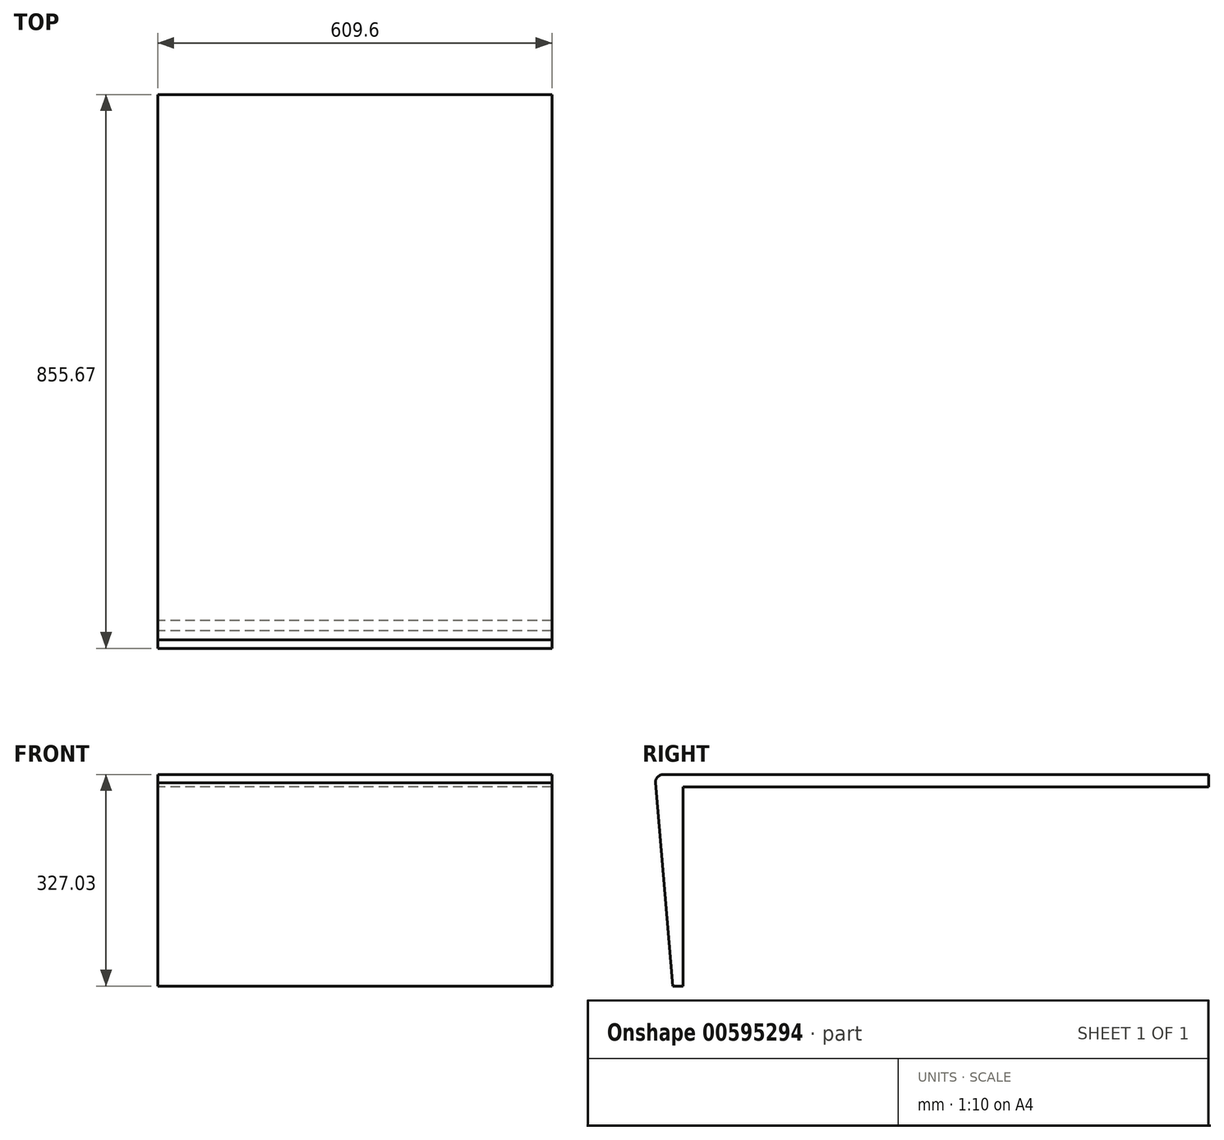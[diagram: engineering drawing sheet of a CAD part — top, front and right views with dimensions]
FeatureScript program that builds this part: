
annotation { "Feature Type Name" : "Feature", "Feature Type Description" : "" }
export const myFeature = defineFeature(function(context is Context, id is Id, definition is map)
    precondition{}
    {
        {
            var Q0;
            Q0=qCreatedBy(makeId("Right.planeOp"),FACE);
            var sketch = newSketch(context, id + "F0", { "sketchPlane" : qUnion([Q0])});
            skLineSegment(sketch, "E0", {"start": v(0, 0) * mm, "end": v(812.8, 0) * mm});
            skLineSegment(sketch, "E1", {"start": v(0, 0) * mm, "end": v(0, -307.98) * mm});
            skLineSegment(sketch, "E2", {"start": v(0, -307.98) * mm, "end": v(-15.87, -307.98) * mm});
            skLineSegment(sketch, "E3", {"start": v(-15.87, -307.98) * mm, "end": v(-42.86, 5.82) * mm});
            skLineSegment(sketch, "E4", {"start": v(-29.86, 19.05) * mm, "end": v(812.8, 19.05) * mm});
            skLineSegment(sketch, "E5", {"start": v(812.8, 19.05) * mm, "end": v(812.8, 0) * mm});
            skArc(sketch, "E6", {"start": v(-29.86, 19.05) * mm, "mid": v(-39.23, 15.26) * mm, "end": v(-42.86, 5.82) * mm});
            skPoint(sketch, "E6.first.point", {"position": v(-42.86, 5.82) * mm});
            skPoint(sketch, "E6.second.point", {"position": v(-29.86, 19.05) * mm});
            skPoint(sketch, "E6.third.point", {"position": v(-24.34, -4.93) * mm});
            skSolve(sketch);
        }
        {
            var Q0;
            Q0=makeQuery(id+"F0.imprint","IMPRINT",FACE,{"disambiguationData":[TD([[makeQuery(id+"F0.imprint","IMPRINT",EDGE,{"derivedFrom":sQuery(id+"F0.wireOp",EDGE,"E0")}),1.0]])]});
            extrude(context, id + "F1", {"entities" : qUnion([Q0]), "depth" : 609.6 * mm, "offsetDistance" : 25.4 * mm});
        }
    });
